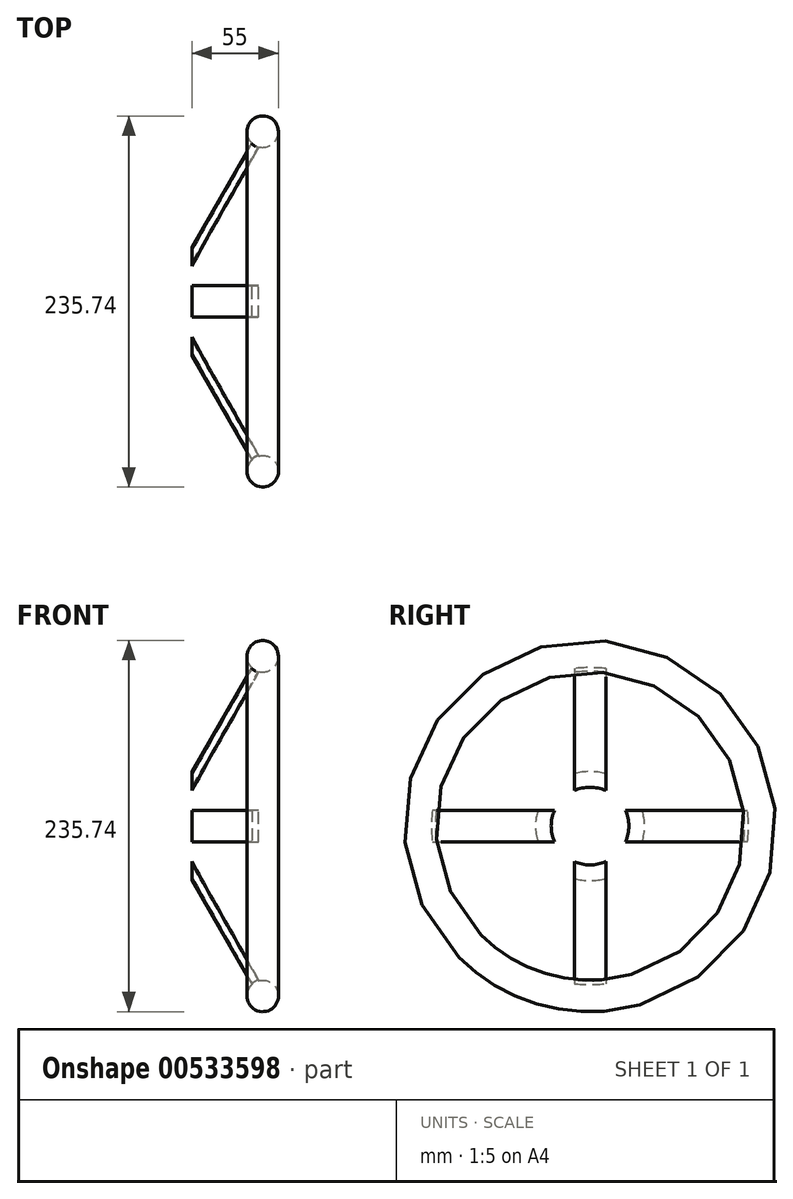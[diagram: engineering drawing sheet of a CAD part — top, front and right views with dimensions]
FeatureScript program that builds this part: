
annotation { "Feature Type Name" : "Feature", "Feature Type Description" : "" }
export const myFeature = defineFeature(function(context is Context, id is Id, definition is map)
    precondition{}
    {
        {
            var Q0;
            Q0=qCreatedBy(makeId("Front.planeOp"),FACE);
            var sketch = newSketch(context, id + "F0", { "sketchPlane" : qUnion([Q0])});
            skLineSegment(sketch, "E0", {"start": v(0, 0) * mm, "end": v(59.18, 102.5) * mm});
            skLineSegment(sketch, "E1", {"start": v(59.18, 102.5) * mm, "end": v(63.5, 100) * mm});
            skLineSegment(sketch, "E2", {"start": v(63.5, 100) * mm, "end": v(5.77, 0) * mm});
            skLineSegment(sketch, "E3", {"start": v(5.77, 0) * mm, "end": v(0, 0) * mm});
            skLineSegment(sketch, "E4", {"start": v(-27.25, 0) * mm, "end": v(68.36, 0) * mm});
            skSolve(sketch);
        }
        {
            var Q0;
            {var subQ0=sQuery(id+"F0.wireOp",EDGE,"E0");Q0=makeQuery(id+"F0.imprint","IMPRINT",FACE,{"disambiguationData":[TD([[makeQuery(id+"F0.imprint","IMPRINT",EDGE,{"derivedFrom":subQ0}),-1.0]])]});}
            var Q1;
            Q1=sQuery(id+"F0.wireOp",EDGE,"E4");
            revolve(context, id + "F1", {"entities" : qUnion([Q0]), "axis" : qUnion([Q1]), "revolveType" : RevolveType.FULL});
        }
        {
            var Q0;
            Q0=qCreatedBy(makeId("Right.planeOp"),FACE);
            var sketch = newSketch(context, id + "F2", { "sketchPlane" : qUnion([Q0])});
            skLineSegment(sketch, "E5.bottom", {"start": v(10, 110) * mm, "end": v(110, 110) * mm});
            skLineSegment(sketch, "E5.top", {"start": v(10, 10) * mm, "end": v(110, 10) * mm});
            skLineSegment(sketch, "E5.left", {"start": v(10, 110) * mm, "end": v(10, 10) * mm});
            skLineSegment(sketch, "E5.right", {"start": v(110, 110) * mm, "end": v(110, 10) * mm});
            skLineSegment(sketch, "E6.bottom", {"start": v(110, -10) * mm, "end": v(10, -10) * mm});
            skLineSegment(sketch, "E6.top", {"start": v(110, -110) * mm, "end": v(10, -110) * mm});
            skLineSegment(sketch, "E6.left", {"start": v(110, -10) * mm, "end": v(110, -110) * mm});
            skLineSegment(sketch, "E6.right", {"start": v(10, -10) * mm, "end": v(10, -110) * mm});
            skLineSegment(sketch, "E7.bottom", {"start": v(-10, 110) * mm, "end": v(-110, 110) * mm});
            skLineSegment(sketch, "E7.top", {"start": v(-10, 10) * mm, "end": v(-110, 10) * mm});
            skLineSegment(sketch, "E7.left", {"start": v(-10, 110) * mm, "end": v(-10, 10) * mm});
            skLineSegment(sketch, "E7.right", {"start": v(-110, 110) * mm, "end": v(-110, 10) * mm});
            skLineSegment(sketch, "E8.bottom", {"start": v(-110, -10) * mm, "end": v(-10, -10) * mm});
            skLineSegment(sketch, "E8.top", {"start": v(-110, -110) * mm, "end": v(-10, -110) * mm});
            skLineSegment(sketch, "E8.left", {"start": v(-110, -10) * mm, "end": v(-110, -110) * mm});
            skLineSegment(sketch, "E8.right", {"start": v(-10, -10) * mm, "end": v(-10, -110) * mm});
            skSolve(sketch);
        }
        {
            var Q0;
            Q0=qSketchRegion(id+"F2",true);
            extrude(context, id + "F3", {"entities" : qUnion([Q0]), "operationType" : NewBodyOperationType.REMOVE, "depth" : 100 * mm});
        }
        {
            var Q0;
            Q0=qCreatedBy(makeId("Front.planeOp"),FACE);
            var sketch = newSketch(context, id + "F4", { "sketchPlane" : qUnion([Q0])});
            skCircle(sketch, "E9", {"center": v(65, 107.87) * mm, "radius": 10 * mm});
            skLineSegment(sketch, "E10", {"start": v(-27.25, 0) * mm, "end": v(85.64, 0) * mm});
            skSolve(sketch);
        }
        {
            var Q0;
            Q0=makeQuery(id+"F4.imprint","IMPRINT",FACE,{"disambiguationData":[TD([[makeQuery(id+"F4.imprint","IMPRINT",EDGE,{"derivedFrom":sQuery(id+"F4.wireOp",EDGE,"E9")}),1.0]])]});
            var Q1;
            Q1=sQuery(id+"F4.wireOp",EDGE,"E10");
            revolve(context, id + "F5", {"operationType" : NewBodyOperationType.ADD, "entities" : qUnion([Q0]), "axis" : qUnion([Q1]), "revolveType" : RevolveType.FULL});
        }
        {
            var Q0;
            Q0=qCreatedBy(makeId("Front.planeOp"),FACE);
            var sketch = newSketch(context, id + "F6", { "sketchPlane" : qUnion([Q0])});
            skLineSegment(sketch, "E11.bottom", {"start": v(-76.77, 93.62) * mm, "end": v(20, 93.62) * mm});
            skLineSegment(sketch, "E11.top", {"start": v(-76.77, -103.8) * mm, "end": v(20, -103.8) * mm});
            skLineSegment(sketch, "E11.left", {"start": v(-76.77, 93.62) * mm, "end": v(-76.77, -103.8) * mm});
            skLineSegment(sketch, "E11.right", {"start": v(20, 93.62) * mm, "end": v(20, -103.8) * mm});
            skSolve(sketch);
        }
        {
            var Q0;
            Q0=qSketchRegion(id+"F6",true);
            extrude(context, id + "F7", {"entities" : qUnion([Q0]), "operationType" : NewBodyOperationType.REMOVE, "oppositeDirection" : true, "depth" : 100 * mm, "symmetric" : true});
        }
    });
